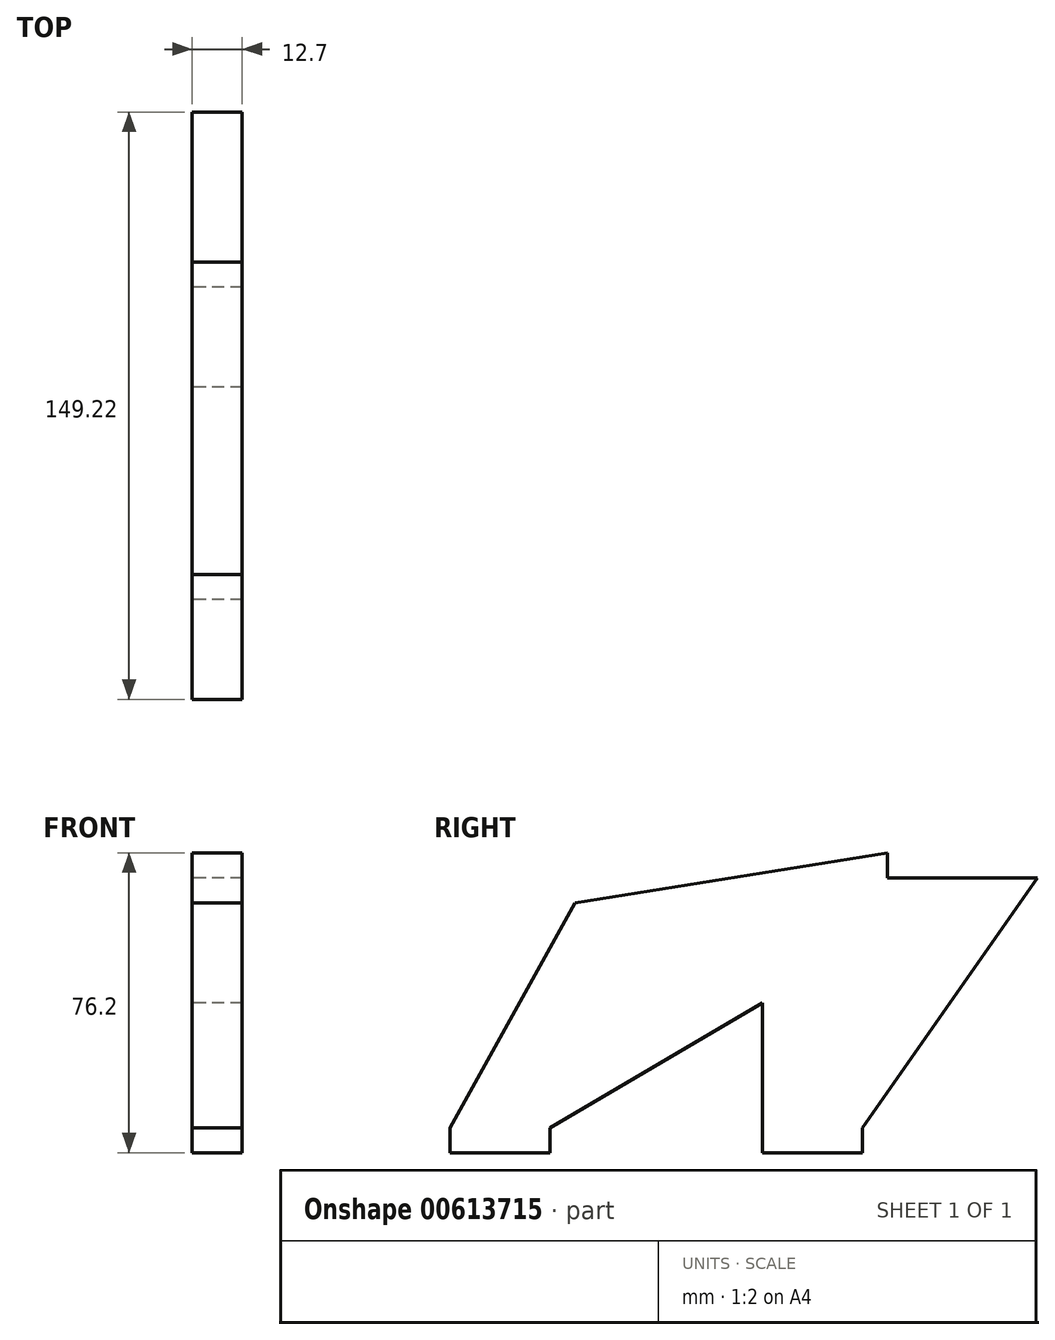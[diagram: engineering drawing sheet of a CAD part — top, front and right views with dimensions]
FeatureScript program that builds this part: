
annotation { "Feature Type Name" : "Feature", "Feature Type Description" : "" }
export const myFeature = defineFeature(function(context is Context, id is Id, definition is map)
    precondition{}
    {
        {
            var Q0;
            Q0=qCreatedBy(makeId("Right.planeOp"),FACE);
            var sketch = newSketch(context, id + "F0", { "sketchPlane" : qUnion([Q0])});
            skLineSegment(sketch, "E0.top", {"start": v(-66.91, -6.35) * mm, "end": v(-41.51, -6.35) * mm});
            skLineSegment(sketch, "E0.left", {"start": v(-66.91, 0) * mm, "end": v(-66.91, -6.35) * mm});
            skLineSegment(sketch, "E0.right", {"start": v(-41.51, 0) * mm, "end": v(-41.51, -6.35) * mm});
            skLineSegment(sketch, "E1.top", {"start": v(12.46, -6.35) * mm, "end": v(37.86, -6.35) * mm});
            skLineSegment(sketch, "E1.left", {"start": v(12.46, 0) * mm, "end": v(12.46, -6.35) * mm});
            skLineSegment(sketch, "E1.right", {"start": v(37.86, 0) * mm, "end": v(37.86, -6.35) * mm});
            skLineSegment(sketch, "E2.top", {"start": v(44.21, 63.5) * mm, "end": v(82.31, 63.5) * mm});
            skLineSegment(sketch, "E2.left", {"start": v(44.21, 69.85) * mm, "end": v(44.21, 63.5) * mm});
            skLineSegment(sketch, "E3", {"start": v(-66.91, 0) * mm, "end": v(-35.16, 57.15) * mm});
            skLineSegment(sketch, "E4", {"start": v(37.86, 0) * mm, "end": v(82.31, 63.5) * mm});
            skLineSegment(sketch, "E5", {"start": v(44.21, 69.85) * mm, "end": v(-35.16, 57.15) * mm});
            skLineSegment(sketch, "E6", {"start": v(12.46, 0) * mm, "end": v(12.46, 31.75) * mm});
            skLineSegment(sketch, "E7", {"start": v(12.46, 31.75) * mm, "end": v(-41.51, 0) * mm});
            skSolve(sketch);
        }
        {
            var Q0;
            Q0=makeQuery(id+"F0.imprint","IMPRINT",FACE,{"disambiguationData":[TD([[makeQuery(id+"F0.imprint","IMPRINT",EDGE,{"derivedFrom":sQuery(id+"F0.wireOp",EDGE,"E0.top")}),1.0]])]});
            extrude(context, id + "F1", {"entities" : qUnion([Q0]), "depth" : 12.7 * mm, "offsetDistance" : 25.4 * mm});
        }
    });
